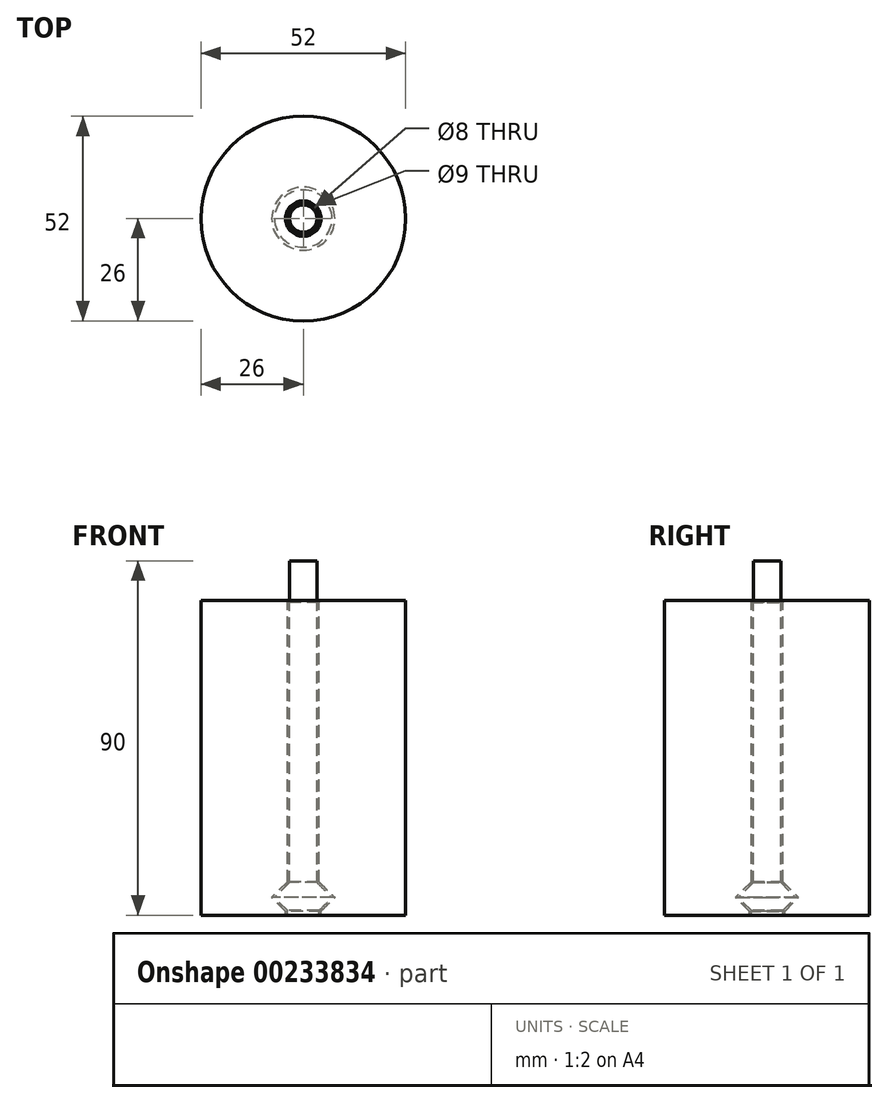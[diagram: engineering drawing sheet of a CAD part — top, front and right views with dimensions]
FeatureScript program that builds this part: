
annotation { "Feature Type Name" : "Feature", "Feature Type Description" : "" }
export const myFeature = defineFeature(function(context is Context, id is Id, definition is map)
    precondition{}
    {
        {
            var Q0;
            Q0=qCreatedBy(makeId("Front.planeOp"),FACE);
            var sketch = newSketch(context, id + "F0", { "sketchPlane" : qUnion([Q0])});
            skLineSegment(sketch, "E0.bottom", {"start": v(0, 0) * mm, "end": v(26, 0) * mm});
            skLineSegment(sketch, "E0.top", {"start": v(0, -80) * mm, "end": v(26, -80) * mm});
            skLineSegment(sketch, "E0.left", {"start": v(0, 0) * mm, "end": v(0, -80) * mm, "construction": true});
            skLineSegment(sketch, "E0.right", {"start": v(26, 0) * mm, "end": v(26, -80) * mm});
            skLineSegment(sketch, "E1", {"start": v(3.5, -80) * mm, "end": v(4.5, -79) * mm, "construction": true});
            skLineSegment(sketch, "E2", {"start": v(8, -75.5) * mm, "end": v(4, -71.5) * mm});
            skLineSegment(sketch, "E3", {"start": v(-67, -0.5) * mm, "end": v(7.8, -0.5) * mm, "construction": true});
            skLineSegment(sketch, "E4", {"start": v(4.5, -79) * mm, "end": v(4.5, -80) * mm});
            skLineSegment(sketch, "E5", {"start": v(4.5, -79) * mm, "end": v(7, -76.5) * mm});
            skLineSegment(sketch, "E6", {"start": v(4, -71.5) * mm, "end": v(4, -0.5) * mm});
            skLineSegment(sketch, "E7.trimOffspring", {"start": v(4, -0.5) * mm, "end": v(4.5, 0) * mm});
            skLineSegment(sketch, "E8", {"start": v(7, -76.5) * mm, "end": v(8, -75.5) * mm});
            skPoint(sketch, "E8.endSnap0", {"position": v(8, -76.5) * mm});
            skPoint(sketch, "E9.orphan", {"position": v(9, -76.5) * mm});
            skSolve(sketch);
        }
        {
            var Q0;
            Q0=qCreatedBy(makeId("Front.planeOp"),FACE);
            var sketch = newSketch(context, id + "F1", { "sketchPlane" : qUnion([Q0])});
            skLineSegment(sketch, "E10.0", {"start": v(4, -71.5) * mm, "end": v(4, -0.5) * mm, "construction": true});
            skLineSegment(sketch, "E10.1", {"start": v(4.5, -79) * mm, "end": v(7, -76.5) * mm, "construction": true});
            skLineSegment(sketch, "E10.2", {"start": v(8, -75.5) * mm, "end": v(4, -71.5) * mm, "construction": true});
            skLineSegment(sketch, "E10.3", {"start": v(-67, -0.5) * mm, "end": v(7.8, -0.5) * mm, "construction": true});
            skLineSegment(sketch, "E10.4", {"start": v(4, -0.5) * mm, "end": v(4.5, 0) * mm, "construction": true});
            skLineSegment(sketch, "E10.5", {"start": v(0, 0) * mm, "end": v(0, -80) * mm, "construction": true});
            skLineSegment(sketch, "E10.6", {"start": v(26, 0) * mm, "end": v(26, -80) * mm, "construction": true});
            skLineSegment(sketch, "E10.7", {"start": v(0, 0) * mm, "end": v(26, 0) * mm, "construction": true});
            skLineSegment(sketch, "E10.8", {"start": v(0, -80) * mm, "end": v(26, -80) * mm, "construction": true});
            skLineSegment(sketch, "E10.9", {"start": v(4.5, -79) * mm, "end": v(4.5, -80) * mm, "construction": true});
            skLineSegment(sketch, "E10.10", {"start": v(3.5, -80) * mm, "end": v(4.5, -79) * mm, "construction": true});
            skLineSegment(sketch, "E10.11", {"start": v(7, -76.5) * mm, "end": v(8, -75.5) * mm, "construction": true});
            skLineSegment(sketch, "E11.0", {"start": v(3.5, -0.3) * mm, "end": v(3.8, 0) * mm});
            skLineSegment(sketch, "E11.1", {"start": v(4, -78.8) * mm, "end": v(4, -80) * mm});
            skLineSegment(sketch, "E11.2", {"start": v(4, -78.8) * mm, "end": v(7.3, -75.5) * mm});
            skLineSegment(sketch, "E11.3", {"start": v(7.3, -75.5) * mm, "end": v(3.5, -71.7) * mm});
            skLineSegment(sketch, "E11.4", {"start": v(3.5, -71.7) * mm, "end": v(3.5, -0.3) * mm});
            skLineSegment(sketch, "E12", {"start": v(4, -80) * mm, "end": v(0, -80) * mm});
            skLineSegment(sketch, "E13", {"start": v(3.8, 0) * mm, "end": v(0, 0) * mm});
            skLineSegment(sketch, "E14", {"start": v(0, 0) * mm, "end": v(0, -80) * mm});
            skLineSegment(sketch, "E15", {"start": v(3.5, -0.3) * mm, "end": v(3.5, 0) * mm});
            skSolve(sketch);
        }
        {
            var Q0;
            {var subQ0=sQuery(id+"F0.wireOp",EDGE,"E0.right");Q0=makeQuery(id+"F0.imprint","IMPRINT",FACE,{"disambiguationData":[TD([[makeQuery(id+"F0.imprint","IMPRINT",EDGE,{"derivedFrom":subQ0}),-1.0]])]});}
            var Q1;
            Q1=sQuery(id+"F1.wireOp",EDGE,"E14");
            revolve(context, id + "F2", {"entities" : qUnion([Q0]), "axis" : qUnion([Q1]), "revolveType" : RevolveType.FULL});
        }
        {
            var Q0;
            Q0=makeQuery(id+"F1.imprint","IMPRINT",FACE,{"disambiguationData":[TD([[makeQuery(id+"F1.imprint","IMPRINT",EDGE,{"derivedFrom":sQuery(id+"F1.wireOp",EDGE,"E11.1")}),-1.0]])]});
            var Q1;
            Q1=sQuery(id+"F1.wireOp",EDGE,"E14");
            revolve(context, id + "F3", {"entities" : qUnion([Q0]), "axis" : qUnion([Q1]), "revolveType" : RevolveType.FULL});
        }
        {
            var Q0;
            Q0=makeQuery(id+"F3.opRevolve","SWEPT_FACE",FACE,{"disambiguationData":[OSD([sQuery(id+"F1.wireOp",EDGE,"E13")])]});
            extrude(context, id + "F4", {"entities" : qUnion([Q0]), "operationType" : NewBodyOperationType.ADD, "depth" : 10 * mm});
        }
    });
